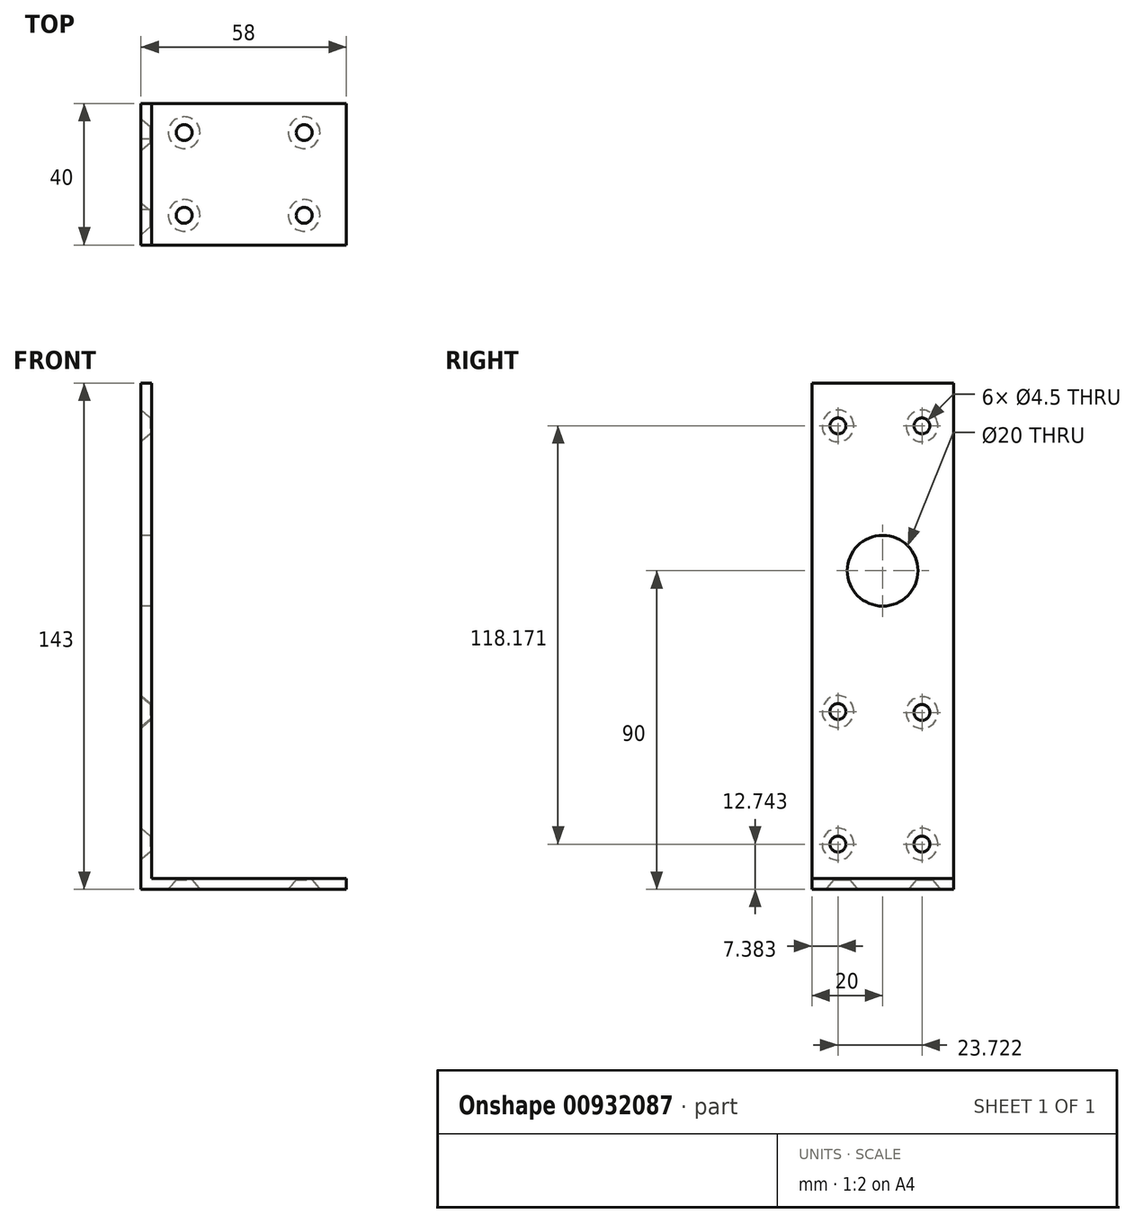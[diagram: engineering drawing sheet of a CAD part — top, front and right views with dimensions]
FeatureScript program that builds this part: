
annotation { "Feature Type Name" : "Feature", "Feature Type Description" : "" }
export const myFeature = defineFeature(function(context is Context, id is Id, definition is map)
    precondition{}
    {
        {
            var Q0;
            Q0=qCreatedBy(makeId("Front.planeOp"),FACE);
            var sketch = newSketch(context, id + "F0", { "sketchPlane" : qUnion([Q0])});
            skLineSegment(sketch, "E0", {"start": v(0, 143) * mm, "end": v(0, 0) * mm});
            skLineSegment(sketch, "E1", {"start": v(0, 0) * mm, "end": v(58, 0) * mm});
            skLineSegment(sketch, "E2", {"start": v(58, 0) * mm, "end": v(58, 3) * mm});
            skLineSegment(sketch, "E3", {"start": v(58, 3) * mm, "end": v(3, 3) * mm});
            skLineSegment(sketch, "E4", {"start": v(3, 3) * mm, "end": v(3, 143) * mm});
            skLineSegment(sketch, "E5", {"start": v(3, 143) * mm, "end": v(0, 143) * mm});
            skSolve(sketch);
        }
        {
            var Q0;
            Q0 = qSketchRegion(id + "F0", true);
            extrude(context, id + "F1", {"entities" : qUnion([Q0]), "depth" : 40 * mm, "offsetDistance" : 25 * mm});
        }
        {
            var Q0;
            Q0=makeQuery(id+"F1.opExtrude","SWEPT_FACE",FACE,{"disambiguationData":[OSD([sQuery(id+"F0.wireOp",EDGE,"E1")])]});
            var sketch = newSketch(context, id + "F2", { "sketchPlane" : qUnion([Q0])});
            skLineSegment(sketch, "E6", {"start": v(0, 40) * mm, "end": v(58, 0) * mm, "construction": true});
            skLineSegment(sketch, "E7", {"start": v(58, 40) * mm, "end": v(0, 0) * mm, "construction": true});
            skLineSegment(sketch, "E8.bottom", {"start": v(12.2, 31.6) * mm, "end": v(46.08, 31.6) * mm, "construction": true});
            skLineSegment(sketch, "E8.top", {"start": v(12.2, 8.22) * mm, "end": v(46.08, 8.22) * mm, "construction": true});
            skLineSegment(sketch, "E8.left", {"start": v(12.2, 31.6) * mm, "end": v(12.2, 8.22) * mm, "construction": true});
            skLineSegment(sketch, "E8.right", {"start": v(46.08, 31.6) * mm, "end": v(46.08, 8.22) * mm, "construction": true});
            skPoint(sketch, "E9", {"position": v(12.2, 31.6) * mm});
            skPoint(sketch, "E10", {"position": v(12.2, 8.22) * mm});
            skPoint(sketch, "E11", {"position": v(46.08, 8.22) * mm});
            skPoint(sketch, "E12", {"position": v(46.08, 31.6) * mm});
            skSolve(sketch);
        }
        {
            var Q0;
            Q0=makeQuery(id+"F1.opExtrude","SWEPT_FACE",FACE,{"disambiguationData":[OSD([sQuery(id+"F0.wireOp",EDGE,"E0")])]});
            var sketch = newSketch(context, id + "F3", { "sketchPlane" : qUnion([Q0])});
            skLineSegment(sketch, "E13", {"start": v(20, 143) * mm, "end": v(20, 0) * mm, "construction": true});
            skCircle(sketch, "E14", {"center": v(20, 90) * mm, "radius": 10 * mm});
            skLineSegment(sketch, "E15", {"start": v(32.28, 0) * mm, "end": v(32.28, 143) * mm, "construction": true});
            skLineSegment(sketch, "E16", {"start": v(8.8, 0) * mm, "end": v(8.8, 143) * mm, "construction": true});
            skPoint(sketch, "E17", {"position": v(32.28, 15.73) * mm});
            skPoint(sketch, "E18", {"position": v(8.8, 15.73) * mm});
            skPoint(sketch, "E19", {"position": v(32.28, 60.4) * mm});
            skPoint(sketch, "E20", {"position": v(8.8, 60.4) * mm});
            skSolve(sketch);
        }
        {
            var Q0;
            Q0=makeQuery(id+"F3.imprint","IMPRINT",FACE,{"disambiguationData":[TD([[makeQuery(id+"F3.imprint","IMPRINT",EDGE,{"derivedFrom":sQuery(id+"F3.wireOp",EDGE,"E14")}),1.0]])]});
            var Q1;
            Q1 = qSketchRegion(id + "F5", true);
            extrude(context, id + "F4", {"entities" : qUnion([Q0, Q1]), "operationType" : NewBodyOperationType.REMOVE, "endBound" : BoundingType.THROUGH_ALL, "oppositeDirection" : true, "depth" : 25 * mm, "offsetDistance" : 25 * mm});
        }
        {
            var Q0;
            Q0=makeQuery(id+"F1.opExtrude","SWEPT_FACE",FACE,{"disambiguationData":[OSD([sQuery(id+"F0.wireOp",EDGE,"E0")])]});
            var sketch = newSketch(context, id + "F5", { "sketchPlane" : qUnion([Q0])});
            skLineSegment(sketch, "E21", {"start": v(32.62, 0) * mm, "end": v(32.62, 143) * mm, "construction": true});
            skLineSegment(sketch, "E22", {"start": v(8.9, 0) * mm, "end": v(8.9, 143) * mm, "construction": true});
            skPoint(sketch, "E23", {"position": v(32.62, 12.74) * mm});
            skPoint(sketch, "E24", {"position": v(8.9, 12.74) * mm});
            skPoint(sketch, "E25", {"position": v(8.9, 49.94) * mm});
            skPoint(sketch, "E26", {"position": v(32.62, 50.21) * mm});
            skPoint(sketch, "E27", {"position": v(8.9, 130.91) * mm});
            skPoint(sketch, "E28", {"position": v(32.62, 130.91) * mm});
            skSolve(sketch);
        }
        {
            var Q0;
            Q0=sQuery(id+"F5.wireOp",VERTEX,"E26");
            var Q1;
            Q1=sQuery(id+"F5.wireOp",VERTEX,"E23");
            var Q2;
            Q2=sQuery(id+"F5.wireOp",VERTEX,"E24");
            var Q3;
            Q3=sQuery(id+"F5.wireOp",VERTEX,"E25");
            var Q4;
            Q4=sQuery(id+"F5.wireOp",VERTEX,"E28");
            var Q5;
            Q5=sQuery(id+"F5.wireOp",VERTEX,"E27");
            var Q6;
            Q6=makeQuery(id+"F1.opExtrude","SWEPT_BODY",BODY,{"disambiguationData":[OSD([sQuery(id+"F0.wireOp",EDGE,"E0"),sQuery(id+"F0.wireOp",EDGE,"E1"),sQuery(id+"F0.wireOp",EDGE,"E2"),sQuery(id+"F0.wireOp",EDGE,"E3"),sQuery(id+"F0.wireOp",EDGE,"E4"),sQuery(id+"F0.wireOp",EDGE,"E5")])]});
            hole(context, id + "F6", {"style" : HoleStyle.C_SINK, "endStyle" : HoleEndStyle.THROUGH, "holeDiameter" : 4.5 * mm, "cSinkDiameter" : 8.96 * mm, "cSinkAngle" : 80 * degree, "majorDiameter" : 5 * mm, "isTappedThrough" : true, "tappedDepth" : 12 * mm, "tapClearance" : 3, "locations" : qUnion([Q0, Q1, Q2, Q3, Q4, Q5]), "scope" : qUnion([Q6])});
        }
        {
            var Q0;
            Q0=sQuery(id+"F2.wireOp",VERTEX,"E11");
            var Q1;
            Q1=sQuery(id+"F2.wireOp",VERTEX,"E10");
            var Q2;
            Q2=sQuery(id+"F2.wireOp",VERTEX,"E9");
            var Q3;
            Q3=sQuery(id+"F2.wireOp",VERTEX,"E12");
            var Q4;
            Q4=makeQuery(id+"F1.opExtrude","SWEPT_BODY",BODY,{"disambiguationData":[OSD([sQuery(id+"F0.wireOp",EDGE,"E0"),sQuery(id+"F0.wireOp",EDGE,"E1"),sQuery(id+"F0.wireOp",EDGE,"E2"),sQuery(id+"F0.wireOp",EDGE,"E3"),sQuery(id+"F0.wireOp",EDGE,"E4"),sQuery(id+"F0.wireOp",EDGE,"E5")])]});
            hole(context, id + "F7", {"style" : HoleStyle.C_SINK, "endStyle" : HoleEndStyle.THROUGH, "holeDiameter" : 4.5 * mm, "cSinkDiameter" : 8.96 * mm, "cSinkAngle" : 80 * degree, "majorDiameter" : 5 * mm, "isTappedThrough" : true, "tappedDepth" : 12 * mm, "tapClearance" : 3, "locations" : qUnion([Q0, Q1, Q2, Q3]), "scope" : qUnion([Q4])});
        }
    });
